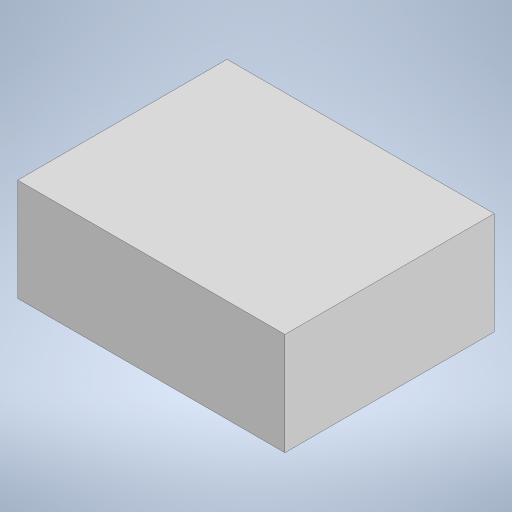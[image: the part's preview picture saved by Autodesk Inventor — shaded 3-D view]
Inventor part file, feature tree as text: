
AUTODESK INVENTOR PART (.ipt)
format: ipt  version: 2023 (Build 270158000, 158)  size: 172,032 bytes
history: native  units: in
note: dims shown in document units (in); Inventor stores cm internally (conversion verified against a paired STEP export)
features: extrude x1, sketch x1
ambient origin geometry x8: Origin, YZ Plane, XZ Plane, XY Plane, X Axis, Y Axis, Z Axis, Center Point
bodies: Solid1 (feature_tree)
feature tree (2):
  extrude  "Extrusion1"  Depth=2.3622in
  sketch  "Sketch1"  dims[d0=1.8504in d1=2.3622in d2=0.9055in d3=0.0in]
